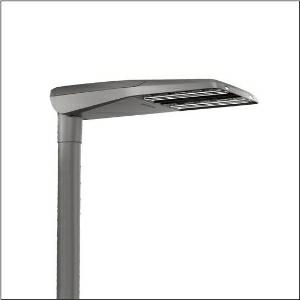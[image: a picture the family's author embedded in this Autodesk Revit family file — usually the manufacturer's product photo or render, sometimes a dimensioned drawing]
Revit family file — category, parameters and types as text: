
# Revit family: streetlight_sl_11_iq_midi___pc-l_5xc3e51f08me_c559
name_source: partatom
category: Lighting Fixtures
units: mm (PartAtom-declared; Revit-internal decimal feet)

## family parameters
Cut with Voids When Loaded = No
Host = Face
Light Source = No
Part Type = Normal
Room Calculation Point = No
Round Connector Dimension = Use Diameter
Shared = No

## types (1)
- --- (1 x LED, 15540 lm, 124.7 W, 3000K)
    Apparent Load = 125 VA
    CIE Flux Codes = 37 73 96 100 100
    Color Rendering = 70
    Color Temperature = 3000K
    Default Elevation = 1800 mm
    Description = Streetlight SL 11 iQ midi, mast luminaire, primary light control with 3 zone facetted reflector, of plastic, silver coated, highly specular, primary optical cover: cover, of PMMA, transparent, light distribution: PC-L, light emission: direct distribution, primary light characteristic: asymmetric, installation type: post-top, side-entry, LED, High Power LED, rated luminous flux: 15.540lm, luminous efficacy: 125lm/W, light colour: 730, colour temperature: 3000K, control: Street-Remote, optimised constant luminous flux control (CLO 2.0), Desk-Remote (wireless, voltage-free reading and setting of iQ features in the workshop via application-optimized NFC function/RFID function), Light-Fading, Smart-Wire, Night-Set, Lumen-Switch, Temp-Guard, Auto-Match, with cable H07RN-F 5x 1.5mm², mains connection: 220..240V, AC, 50/60Hz, connection cable pre-assembled, cable length: 12,5m, start of lifetime: 125W, end of lifetime: 132W, reduction: 57W, luminaire housing, of diecast aluminium, powder-coated, Siteco® metallic grey (DB 702S), length: 780mm, width: 376mm, height: 118mm, spigot size: 60/76mm (post-top) and 42/60/76mm (side-entry), mast flange for spigot size: 42mm: 5XC10008XM4, 60mm: 5XC10008XM2, 76/60mm: 5XC10108XM1, equipment: Power, protection rating (complete): IP66, insulation class (complete): insulation class II (safety insulation), certification: CE, ENEC, VDE, impact resistance: IK09, permissible operating ambient temperature for outdoor applications: -25..+50°C, standard-compliant lighting for roads and squares, packaging unit: 1 piece

Light Distribution: PC-L
    Height = 118 mm
    Lamp = 1 x LED
    Lamp Light Flux = 15540 lm
    Lamp Power = 124.7 W
    Lamp count = 1
    Length = 780 mm
    Luminous efficacy = 125 lm/W
    Manufacturer = Siteco
    ModVariant = No
    Model = 5XC3E51F08ME
    Number of Poles = 1
    OnlyDefault = Yes
    Power Factor = 1
    Product Name = Streetlight SL 11 iQ midi | PC-L
    Product group = mast luminaire | pylon top
    ProductGroupID = 6100
    Protection Class = Protection class II
    Protection Degree = IP 66
    RLX_Detail_Level = 1
    RlxData = <blob elided: 74441 chars, md5=273cdedd>
    Socket = socket
    Standby Power = 0 W
    System Light Flux = 15540 lm
    System Power = 125 W
    Type Comments = factory setting: luminous flux: 100 % | dim-lin: 254 | 557 mA
    Type Image = l_1005960.jpg
    URL = http://relux.com
    VarID = @adj_117931
    Voltage = 0 V
    Weight = 0.00 kg
    Width = 376 mm

## geometry (parser evidence)
native form markers: Blend x4, Sweep x10
no freeform markers — native parametric forms only
